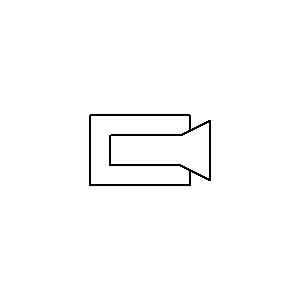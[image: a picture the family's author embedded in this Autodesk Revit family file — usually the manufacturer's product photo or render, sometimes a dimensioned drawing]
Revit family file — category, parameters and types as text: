
# Revit family: Gira_126567
name_source: partatom
category: Electrical Fixtures
revit_build: Autodesk Revit 2017 (Build: 20160225_1515(x64)
units: mm (PartAtom-declared; Revit-internal decimal feet)

## family parameters
Cut with Voids When Loaded = No
Host = Face
Maintain Annotation Orientation = Yes
Part Type = Normal
Room Calculation Point = No
Round Connector Dimension = Use Diameter
Shared = No

## types (1)
- Colour camera door st. Gira TX_44 (WP FM) anthra.
    Available = No
    BIM (1) = https://media.stage.bim.site
    Category = External camera door communication
    Colour = Anthracite
    Data sheet (1) = https://katalog.gira.de
    Default Elevation = 1219 mm
    Description = Colour camera door st. TX_44 AN,Colour camera for door station,,anthracite,Features:,- Installation in a conventional flush-mounted device box.,- Fits in the cover frames of the Gira TX_44 switch range.,- Modular design, allowing easy installation and expandability.,- Signal transmission and supply of the audio and video components via reverse-polarity-protected and short-circuit-proof 2-wire bus.,- Extension of door stations by a colour camera with automatic day or night switching.,- LEDs ensure steady illumination of the field of view at close proximity in night mode.,- Camera can be manually swivelled 20 horizontally and vertically. In combination with the wide-angle lens, a very wide field of view of the door entry area results.,- Automatic background lighting compensation.,- Automatic white balance.,- Automatic gain control (AGC).,- Integrated temperature-dependent camera heating.,- Sprayed-water proof cover plate.,- Camera cover plate made of shock-resistant plastic. Easy to replace if damaged, e.g. due to vandalism.,,Notes :,- The colour camera may not be positioned directly beneath a light.,- Suitable for use in a Gira energy profile.,- Not suitable for use in a Gira energy profile with light.
    GTIN = 4010337265672
    HAN = 126567
    HeinzeBIM = https://bimportal.heinze.de
    Installation technique = Bus system
    Manufacturer = Gira
    Manufacturer URL = https://www.gira.de
    Material = Other
    Mounting method = Built-in
    Name = Colour camera door st. Gira TX_44 (WP FM) anthra.
    URL = http://katalog.gira.de

## geometry (parser evidence)
native form markers: Sweep x2
no freeform markers — native parametric forms only
